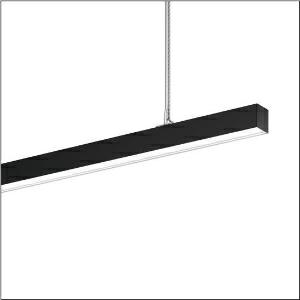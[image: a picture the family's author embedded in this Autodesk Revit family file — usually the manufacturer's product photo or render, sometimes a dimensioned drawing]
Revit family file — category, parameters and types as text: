
# Revit family: silica_r__21_51mx30dc39bb_25b6
name_source: partatom
category: Lighting Fixtures
units: mm (PartAtom-declared; Revit-internal decimal feet)

## family parameters
Cut with Voids When Loaded = No
Host = Face
Light Source = No
Part Type = Normal
Room Calculation Point = No
Round Connector Dimension = Use Diameter
Shared = No

## types (1)
- --- (1 x LED, 10520 lm, 68.3 W, 3000K)
    Apparent Load = 68 VA
    CIE Flux Codes = 47 79 96 57 100
    Color Rendering = 80
    Color Temperature = 3000K
    Default Elevation = 1800 mm
    Description = Silica® 21, office luminaire, primary optical cover: cover, of PMMA, opal, light emission: direct/indirect distribution, primary light characteristic: symmetric, installation type: suspended mounting, LED, rated luminous flux: 10.520lm, luminous efficacy: 154lm/W, light colour: 830, colour temperature: 3000K, with terminal, 3+2-pole, max. 2.5mm², mains connection: 220..240V, AC, 50/60Hz, rated input power: 68.3W, luminaire housing, of aluminium, jet black (RAL 9005), length: 3.004mm, width: 53mm, height: 53mm, protection rating (complete): IP20, insulation class (complete): insulation class I (protective earthing), certification: CE, permissible operating ambient temperature: 0..+35°C, standard: EN 50419, packaging unit: 1 piece
    Height = 53 mm
    Lamp = 1 x LED
    Lamp Light Flux = 10520 lm
    Lamp Power = 68.3 W
    Lamp count = 1
    Length = 3004 mm
    Luminous efficacy = 154 lm/W
    Manufacturer = Siteco
    ModVariant = No
    Model = 51MX30DC39BB
    Mounting Place = Ceiling
    Mounting Type = Pendant
    Number of Poles = 1
    OnlyDefault = Yes
    Power Factor = 1
    Product Name = Silica® 21
    Product group = office luminaire | ceiling pendant
    ProductGroupID = 902
    Protection Class = Protection class I
    Protection Degree = IP 20
    RLX_Detail_Level = 1
    RLX_Emergency_Light_Flux = 0 lm
    RLX_Emergency_Type = 0
    RLX_Emergency_Type_DB = No
    RlxData = <blob elided: 26037 chars, md5=c2adce7d>
    Socket = socket
    Standby Power = 0 W
    System Light Flux = 10520 lm
    System Power = 68 W
    Type Comments = factory setting: luminous flux: 100 % | dim-lin: 254 | 233 mA
    Type Image = l_1335856.jpg
    URL = http://relux.com
    VarID = @adj_086073
    Voltage = 0 V
    Weight = 0.00 kg
    Width = 53 mm

## geometry (parser evidence)
native form markers: Blend x4, Sweep x13
no freeform markers — native parametric forms only
